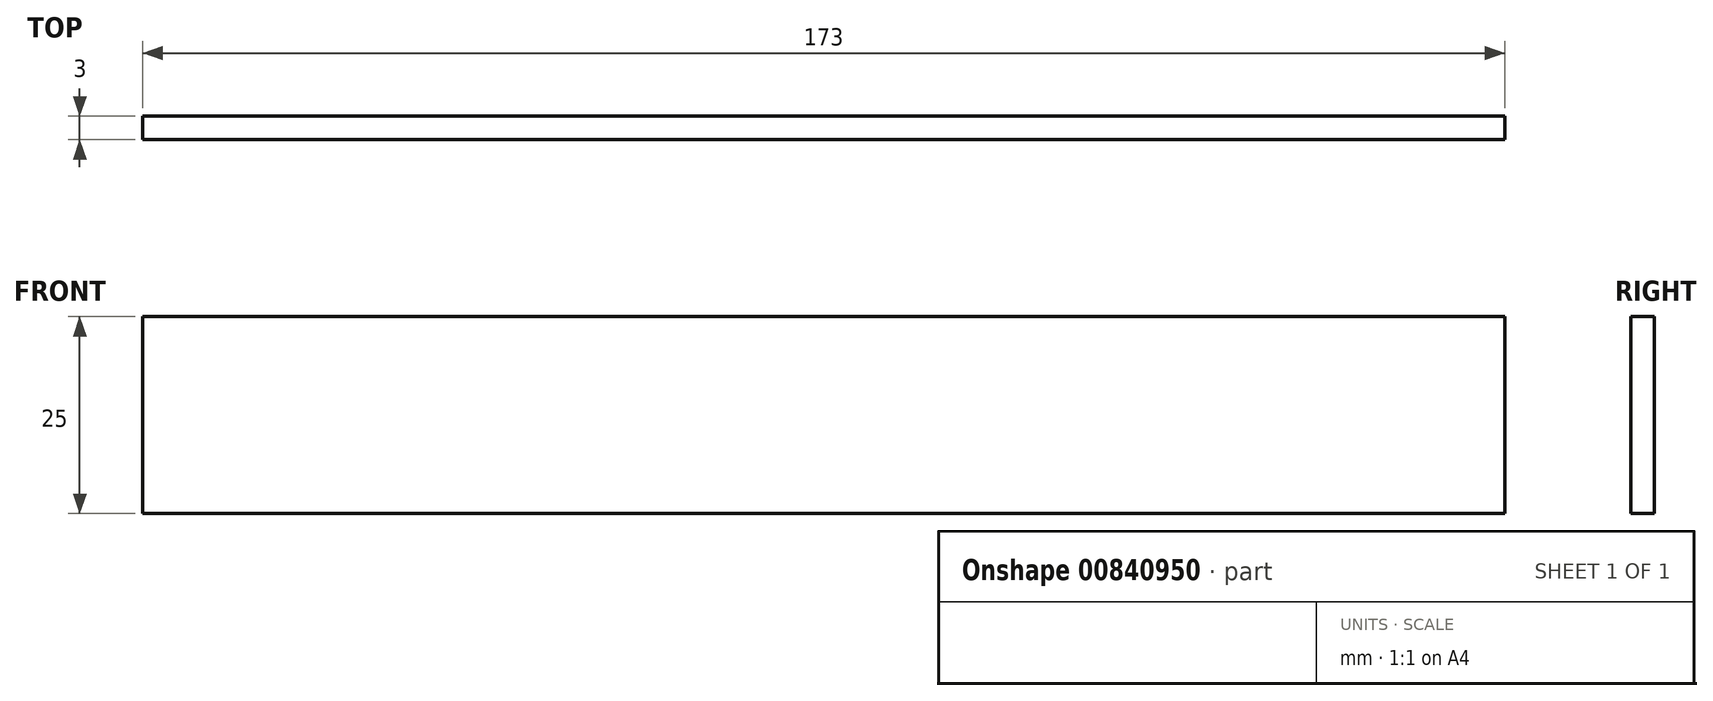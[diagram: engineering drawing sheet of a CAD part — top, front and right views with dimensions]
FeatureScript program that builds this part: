
annotation { "Feature Type Name" : "Feature", "Feature Type Description" : "" }
export const myFeature = defineFeature(function(context is Context, id is Id, definition is map)
    precondition{}
    {
        {
            var Q0;
            Q0=qCreatedBy(makeId("Front.planeOp"),FACE);
            var sketch = newSketch(context, id + "F0", { "sketchPlane" : qUnion([Q0])});
            skLineSegment(sketch, "E0.bottom", {"start": v(1.92, 0) * mm, "end": v(174.92, 0) * mm});
            skLineSegment(sketch, "E0.top", {"start": v(1.92, 25) * mm, "end": v(174.92, 25) * mm});
            skLineSegment(sketch, "E0.left", {"start": v(1.92, 0) * mm, "end": v(1.92, 25) * mm});
            skLineSegment(sketch, "E0.right", {"start": v(174.92, 0) * mm, "end": v(174.92, 25) * mm});
            skSolve(sketch);
        }
        {
            var Q0;
            Q0 = qSketchRegion(id + "F0", true);
            extrude(context, id + "F1", {"entities" : qUnion([Q0]), "depth" : 3 * mm, "offsetDistance" : 25 * mm});
        }
    });
